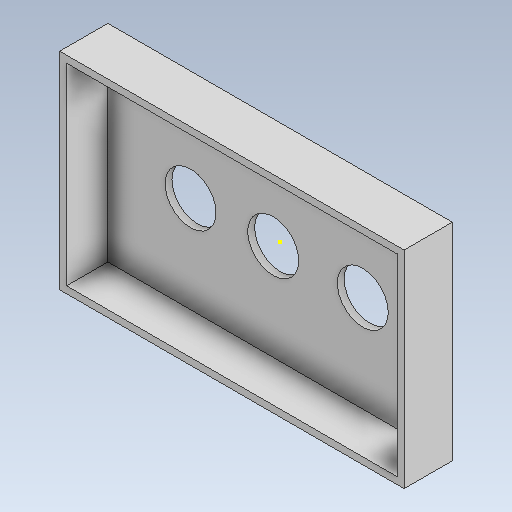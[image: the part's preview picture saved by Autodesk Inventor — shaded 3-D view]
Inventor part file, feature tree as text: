
AUTODESK INVENTOR PART (.ipt)
format: ipt  version: 2021 (Build 250183000, 183)  size: 151,552 bytes
history: native  units: mm
features: sketch x5, extrude x4, projected_geometry x2
ambient origin geometry x8: Origin, YZ Plane, XZ Plane, XY Plane, X Axis, Y Axis, Z Axis, Center Point
bodies: Solid1 (feature_tree)
feature tree (11):
  extrude  "Extrusion1"  Depth=150.0mm
  extrude  "Extrusion2"  Depth=5.0mm
  extrude  "Extrusion3"  Depth=30.0mm
  extrude  "Extrusion4"  TaperAngle=0.0deg  [1 undecoded]
  sketch  "Sketch5"  dims[d15=37.0mm d16=37.0mm d17=125.0mm d18=65.0mm d19=60.0mm d20=75.0mm]
  sketch  "Sketch1"  dims[d0=250.0mm d1=150.0mm]
  sketch  "Sketch2"  dims[d2=5.0mm d3=0.0mm d4=5.0mm]
  projected_geometry  "Projected Loop1"
  sketch  "Sketch3"  dims[d5=30.0mm d6=0.0mm d8=37.0mm]
  projected_geometry  "Projected Loop2"
  sketch  "Sketch4"  dims[d9=50.0mm d10=0.0mm d11=0.0mm d12=0.0mm]
note: 1 required parameter value undecoded (feature->parameter linkage not recoverable at this tier; creation-order binding heuristic only, values carry confidence <= 0.55)
